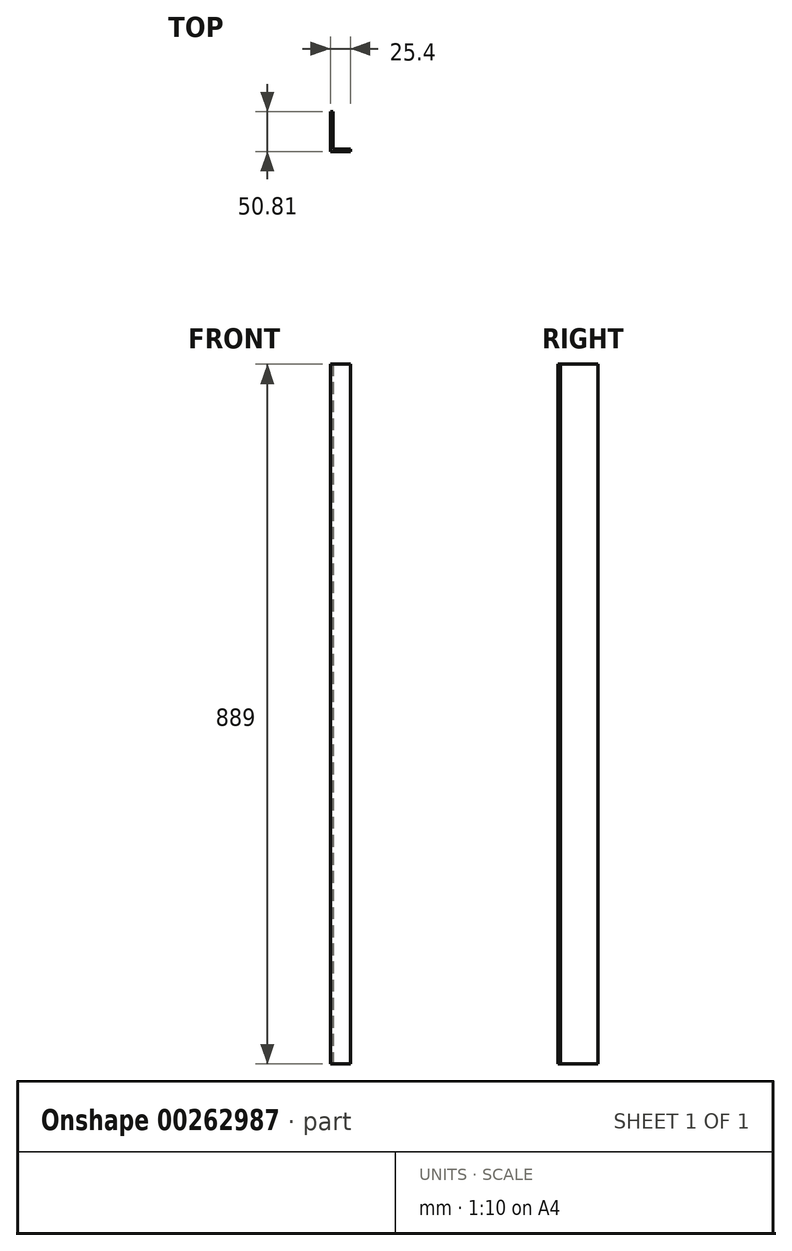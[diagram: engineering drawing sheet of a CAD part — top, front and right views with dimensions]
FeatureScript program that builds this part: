
annotation { "Feature Type Name" : "Feature", "Feature Type Description" : "" }
export const myFeature = defineFeature(function(context is Context, id is Id, definition is map)
    precondition{}
    {
        {
            var Q0;
            Q0=qCreatedBy(makeId("Top.planeOp"),FACE);
            var sketch = newSketch(context, id + "F0", { "sketchPlane" : qUnion([Q0])});
            skLineSegment(sketch, "E0", {"start": v(0, 50.8) * mm, "end": v(0, 0) * mm});
            skLineSegment(sketch, "E1", {"start": v(25.4, 0) * mm, "end": v(0, 0) * mm});
            skLineSegment(sketch, "E2", {"start": v(25.4, 0) * mm, "end": v(25.4, 3.18) * mm});
            skLineSegment(sketch, "E3", {"start": v(3.17, 3.17) * mm, "end": v(3.17, 50.81) * mm});
            skLineSegment(sketch, "E4", {"start": v(3.17, 50.81) * mm, "end": v(0, 50.8) * mm});
            skLineSegment(sketch, "E5", {"start": v(3.17, 3.18) * mm, "end": v(25.4, 3.18) * mm});
            skSolve(sketch);
        }
        {
            var Q0;
            Q0 = qSketchRegion(id + "F0", true);
            extrude(context, id + "F1", {"entities" : qUnion([Q0]), "depth" : 889 * mm});
        }
    });
